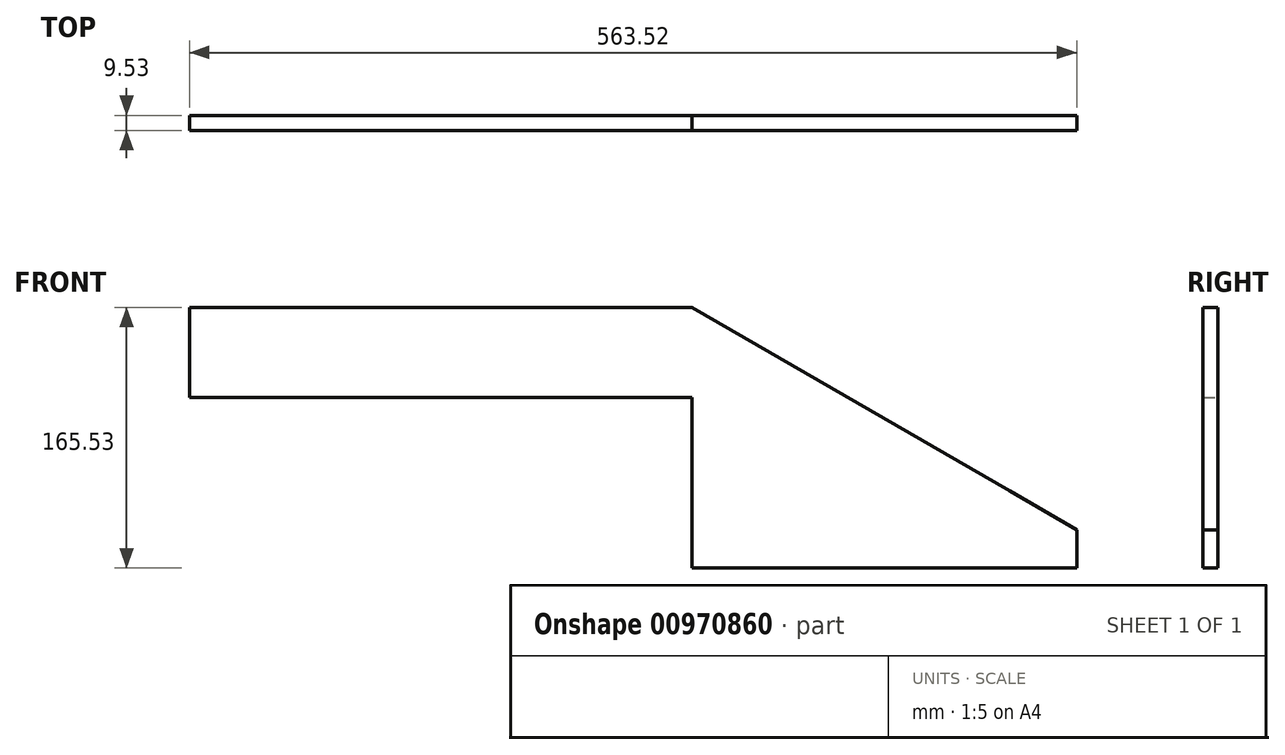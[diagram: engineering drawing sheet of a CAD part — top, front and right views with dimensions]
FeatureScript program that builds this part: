
annotation { "Feature Type Name" : "Feature", "Feature Type Description" : "" }
export const myFeature = defineFeature(function(context is Context, id is Id, definition is map)
    precondition{}
    {
        {
            var Q0;
            Q0=qCreatedBy(makeId("Front.planeOp"),FACE);
            var sketch = newSketch(context, id + "F0", { "sketchPlane" : qUnion([Q0])});
            skLineSegment(sketch, "E0.bottom", {"start": v(-592.75, 52.67) * mm, "end": v(16.85, 52.67) * mm});
            skLineSegment(sketch, "E0.top", {"start": v(-592.75, -48.93) * mm, "end": v(626.45, -48.93) * mm});
            skLineSegment(sketch, "E0.left", {"start": v(-592.75, 52.67) * mm, "end": v(-592.75, -48.93) * mm});
            skLineSegment(sketch, "E0.right", {"start": v(626.45, 52.67) * mm, "end": v(626.45, -48.93) * mm});
            skLineSegment(sketch, "E1.bottom", {"start": v(626.45, 52.67) * mm, "end": v(321.65, 52.67) * mm});
            skLineSegment(sketch, "E1.top", {"start": v(626.45, 116.17) * mm, "end": v(321.65, 116.17) * mm});
            skLineSegment(sketch, "E1.left", {"start": v(626.45, 52.67) * mm, "end": v(626.45, 116.17) * mm});
            skLineSegment(sketch, "E1.right", {"start": v(321.65, 52.67) * mm, "end": v(321.65, 116.17) * mm});
            skLineSegment(sketch, "E2.top", {"start": v(-592.75, 161.05) * mm, "end": v(16.85, 161.05) * mm});
            skLineSegment(sketch, "E2.left", {"start": v(-592.75, 52.67) * mm, "end": v(-592.75, 161.05) * mm});
            skLineSegment(sketch, "E2.right", {"start": v(16.85, 52.67) * mm, "end": v(16.85, 161.05) * mm});
            skLineSegment(sketch, "E3", {"start": v(626.45, 52.67) * mm, "end": v(802.43, -48.93) * mm});
            skLineSegment(sketch, "E4", {"start": v(802.43, -48.93) * mm, "end": v(834.18, 6.06) * mm});
            skLineSegment(sketch, "E5", {"start": v(626.45, 52.67) * mm, "end": v(658.2, 107.66) * mm});
            skLineSegment(sketch, "E6", {"start": v(658.2, 107.66) * mm, "end": v(834.18, 6.06) * mm});
            skLineSegment(sketch, "E7", {"start": v(834.18, 6.06) * mm, "end": v(834.18, 315.51) * mm});
            skLineSegment(sketch, "E8", {"start": v(554.78, 322.17) * mm, "end": v(554.78, 135.22) * mm});
            skLineSegment(sketch, "E9", {"start": v(626.45, 122.52) * mm, "end": v(16.85, 122.52) * mm});
            skLineSegment(sketch, "E10.0", {"start": v(626.45, 135.22) * mm, "end": v(16.85, 135.22) * mm});
            skLineSegment(sketch, "E11.0", {"start": v(665.46, 103.47) * mm, "end": v(655.78, 103.47) * mm});
            skLineSegment(sketch, "E12", {"start": v(16.85, 154.27) * mm, "end": v(16.85, 103.47) * mm});
            skLineSegment(sketch, "E13.trimOffspring", {"start": v(16.85, 154.27) * mm, "end": v(-592.75, 154.27) * mm});
            skLineSegment(sketch, "E14.trimOffspring", {"start": v(16.85, 103.47) * mm, "end": v(-592.75, 103.47) * mm});
            skLineSegment(sketch, "E15", {"start": v(626.45, 116.17) * mm, "end": v(626.45, 116.17) * mm});
            skLineSegment(sketch, "E16", {"start": v(626.45, 122.52) * mm, "end": v(626.45, 135.22) * mm});
            skLineSegment(sketch, "E17", {"start": v(834.18, 6.06) * mm, "end": v(855.85, 43.6) * mm});
            skLineSegment(sketch, "E18", {"start": v(855.85, 43.6) * mm, "end": v(894.18, 21.47) * mm});
            skLineSegment(sketch, "E19", {"start": v(894.18, 21.47) * mm, "end": v(872.45, -16.18) * mm});
            skLineSegment(sketch, "E20", {"start": v(872.45, -16.18) * mm, "end": v(834.18, 6.06) * mm});
            skLineSegment(sketch, "E21", {"start": v(853.31, -5.06) * mm, "end": v(834.18, -38.2) * mm});
            skLineSegment(sketch, "E22.0", {"start": v(-592.75, 46.32) * mm, "end": v(626.45, 46.32) * mm});
            skLineSegment(sketch, "E23.trimOffspring", {"start": v(321.65, 52.67) * mm, "end": v(626.45, 52.67) * mm});
            skLineSegment(sketch, "E24", {"start": v(321.65, 84.42) * mm, "end": v(626.45, 84.42) * mm});
            skLineSegment(sketch, "E25", {"start": v(642.33, 80.17) * mm, "end": v(818.3, -21.43) * mm});
            skLineSegment(sketch, "E26", {"start": v(853.31, -5.06) * mm, "end": v(875.12, 32.47) * mm});
            skLineSegment(sketch, "E27", {"start": v(626.45, 128.87) * mm, "end": v(16.85, 128.87) * mm});
            skLineSegment(sketch, "E28", {"start": v(16.85, 128.87) * mm, "end": v(-592.75, 128.87) * mm});
            skLineSegment(sketch, "E29.0", {"start": v(315.3, 52.67) * mm, "end": v(315.3, 109.82) * mm});
            skLineSegment(sketch, "E30", {"start": v(315.3, 52.67) * mm, "end": v(365.35, 52.67) * mm});
            skLineSegment(sketch, "E31", {"start": v(315.3, 109.82) * mm, "end": v(634.38, 109.82) * mm});
            skLineSegment(sketch, "E32", {"start": v(315.3, 52.67) * mm, "end": v(1006.93, 52.67) * mm});
            skLineSegment(sketch, "E33", {"start": v(634.38, 109.82) * mm, "end": v(634.38, -55.71) * mm});
            skLineSegment(sketch, "E34", {"start": v(880.35, 69.65) * mm, "end": v(877.52, 64.75) * mm});
            skLineSegment(sketch, "E35", {"start": v(877.52, 64.75) * mm, "end": v(779.96, -104.23) * mm});
            skLineSegment(sketch, "E36", {"start": v(634.38, -55.71) * mm, "end": v(824.21, -55.71) * mm});
            skLineSegment(sketch, "E37", {"start": v(634.38, 109.82) * mm, "end": v(836.25, -6.73) * mm});
            skLineSegment(sketch, "E38.0", {"start": v(912.5, 44.56) * mm, "end": v(814.93, -124.42) * mm});
            skLineSegment(sketch, "E39", {"start": v(836.25, -6.73) * mm, "end": v(878.82, -31.47) * mm});
            skLineSegment(sketch, "E40", {"start": v(824.21, -55.71) * mm, "end": v(878.82, -55.71) * mm});
            skLineSegment(sketch, "E41", {"start": v(878.82, -55.71) * mm, "end": v(878.82, -31.47) * mm});
            skSolve(sketch);
        }
        {
            var Q0;
            {var subQ0=sQuery(id+"F0.wireOp",EDGE,"E24");Q0=makeQuery(id+"F0.imprint","IMPRINT",FACE,{"disambiguationData":[TD([[makeQuery(id+"F0.imprint","IMPRINT",EDGE,{"derivedFrom":subQ0}),1.0]])]});}
            var Q1;
            {var subQ1=sQuery(id+"F0.wireOp",EDGE,"E29.0");Q1=makeQuery(id+"F0.imprint","IMPRINT",FACE,{"disambiguationData":[TD([[makeQuery(id+"F0.imprint","IMPRINT",EDGE,{"derivedFrom":subQ1}),-1.0]])]});}
            var Q2;
            {var subQ3=sQuery(id+"F0.wireOp",EDGE,"E24");Q2=makeQuery(id+"F0.imprint","IMPRINT",FACE,{"disambiguationData":[TD([[makeQuery(id+"F0.imprint","IMPRINT",EDGE,{"derivedFrom":subQ3}),-1.0]])]});}
            var Q3;
            {var subQ3=sQuery(id+"F0.wireOp",EDGE,"E1.left");var subQ8=makeQuery(id+"F0.imprint","INTERSECT",VERTEX,{"derivedFrom":[subQ3,sQuery(id+"F0.wireOp",EDGE,"E24")]});Q3=makeQuery(id+"F0.imprint","IMPRINT",FACE,{"disambiguationData":[TD([[makeQuery(id+"F0.imprint","IMPRINT",EDGE,{"disambiguationData":[TD([[subQ8,-1.0]])],"derivedFrom":subQ3}),-1.0]])]});}
            var Q4;
            {var subQ0=sQuery(id+"F0.wireOp",EDGE,"E5");var subQ1=makeQuery(id+"F0.imprint","INTERSECT",VERTEX,{"derivedFrom":[subQ0,sQuery(id+"F0.wireOp",EDGE,"E25")]});Q4=makeQuery(id+"F0.imprint","IMPRINT",FACE,{"disambiguationData":[TD([[makeQuery(id+"F0.imprint","IMPRINT",EDGE,{"disambiguationData":[TD([[subQ1,1.0]])],"derivedFrom":subQ0}),1.0]])]});}
            var Q5;
            {var subQ0=sQuery(id+"F0.wireOp",EDGE,"E25");var subQ1=sQuery(id+"F0.wireOp",EDGE,"E5");var subQ2=makeQuery(id+"F0.imprint","INTERSECT",VERTEX,{"derivedFrom":[subQ1,subQ0]});Q5=makeQuery(id+"F0.imprint","IMPRINT",FACE,{"disambiguationData":[TD([[makeQuery(id+"F0.imprint","IMPRINT",EDGE,{"disambiguationData":[TD([[subQ2,-1.0]])],"derivedFrom":subQ1}),-1.0]])]});}
            var Q6;
            {var subQ0=sQuery(id+"F0.wireOp",EDGE,"E25");var subQ1=sQuery(id+"F0.wireOp",EDGE,"E5");var subQ2=makeQuery(id+"F0.imprint","INTERSECT",VERTEX,{"derivedFrom":[subQ1,subQ0]});Q6=makeQuery(id+"F0.imprint","IMPRINT",FACE,{"disambiguationData":[TD([[makeQuery(id+"F0.imprint","IMPRINT",EDGE,{"disambiguationData":[TD([[subQ2,1.0]])],"derivedFrom":subQ1}),-1.0]])]});}
            var Q7;
            {var subQ1=sQuery(id+"F0.wireOp",EDGE,"E5");var subQ3=sQuery(id+"F0.wireOp",EDGE,"E33");var subQ4=makeQuery(id+"F0.imprint","INTERSECT",VERTEX,{"derivedFrom":[subQ1,subQ3]});Q7=makeQuery(id+"F0.imprint","IMPRINT",FACE,{"disambiguationData":[TD([[makeQuery(id+"F0.imprint","IMPRINT",EDGE,{"disambiguationData":[TD([[subQ4,-1.0]])],"derivedFrom":subQ3}),-1.0]])]});}
            var Q8;
            {var subQ0=sQuery(id+"F0.wireOp",EDGE,"E4");var subQ7=sQuery(id+"F0.wireOp",EDGE,"E3");var subQ9=makeQuery(id+"F0.imprint","INTERSECT",VERTEX,{"derivedFrom":[subQ7,subQ0]});Q8=makeQuery(id+"F0.imprint","IMPRINT",FACE,{"disambiguationData":[TD([[makeQuery(id+"F0.imprint","IMPRINT",EDGE,{"disambiguationData":[TD([[subQ9,1.0]])],"derivedFrom":subQ7}),-1.0]])]});}
            var Q9;
            {var subQ5=sQuery(id+"F0.wireOp",EDGE,"E4");var subQ7=sQuery(id+"F0.wireOp",EDGE,"E3");var subQ8=makeQuery(id+"F0.imprint","INTERSECT",VERTEX,{"derivedFrom":[subQ7,subQ5]});Q9=makeQuery(id+"F0.imprint","IMPRINT",FACE,{"disambiguationData":[TD([[makeQuery(id+"F0.imprint","IMPRINT",EDGE,{"disambiguationData":[TD([[subQ8,1.0]])],"derivedFrom":subQ7}),1.0]])]});}
            var Q10;
            {var subQ0=sQuery(id+"F0.wireOp",EDGE,"E25");var subQ1=sQuery(id+"F0.wireOp",EDGE,"E4");var subQ2=makeQuery(id+"F0.imprint","INTERSECT",VERTEX,{"derivedFrom":[subQ1,subQ0]});Q10=makeQuery(id+"F0.imprint","IMPRINT",FACE,{"disambiguationData":[TD([[makeQuery(id+"F0.imprint","IMPRINT",EDGE,{"disambiguationData":[TD([[subQ2,-1.0]])],"derivedFrom":subQ1}),1.0]])]});}
            var Q11;
            {var subQ6=sQuery(id+"F0.wireOp",EDGE,"E40");var subQ8=sQuery(id+"F0.wireOp",EDGE,"E36");var subQ9=makeQuery(id+"F0.imprint","INTERSECT",VERTEX,{"derivedFrom":[subQ8,subQ6]});Q11=makeQuery(id+"F0.imprint","IMPRINT",FACE,{"disambiguationData":[TD([[makeQuery(id+"F0.imprint","IMPRINT",EDGE,{"disambiguationData":[TD([[subQ9,1.0]])],"derivedFrom":subQ8}),1.0]])]});}
            var Q12;
            {var subQ5=sQuery(id+"F0.wireOp",EDGE,"E41");Q12=makeQuery(id+"F0.imprint","IMPRINT",FACE,{"disambiguationData":[TD([[makeQuery(id+"F0.imprint","IMPRINT",EDGE,{"derivedFrom":subQ5}),1.0]])]});}
            extrude(context, id + "F1", {"entities" : qUnion([Q0, Q1, Q2, Q3, Q4, Q5, Q6, Q7, Q8, Q9, Q10, Q11, Q12]), "depth" : 9.52 * mm, "offsetDistance" : 25.4 * mm});
        }
    });
